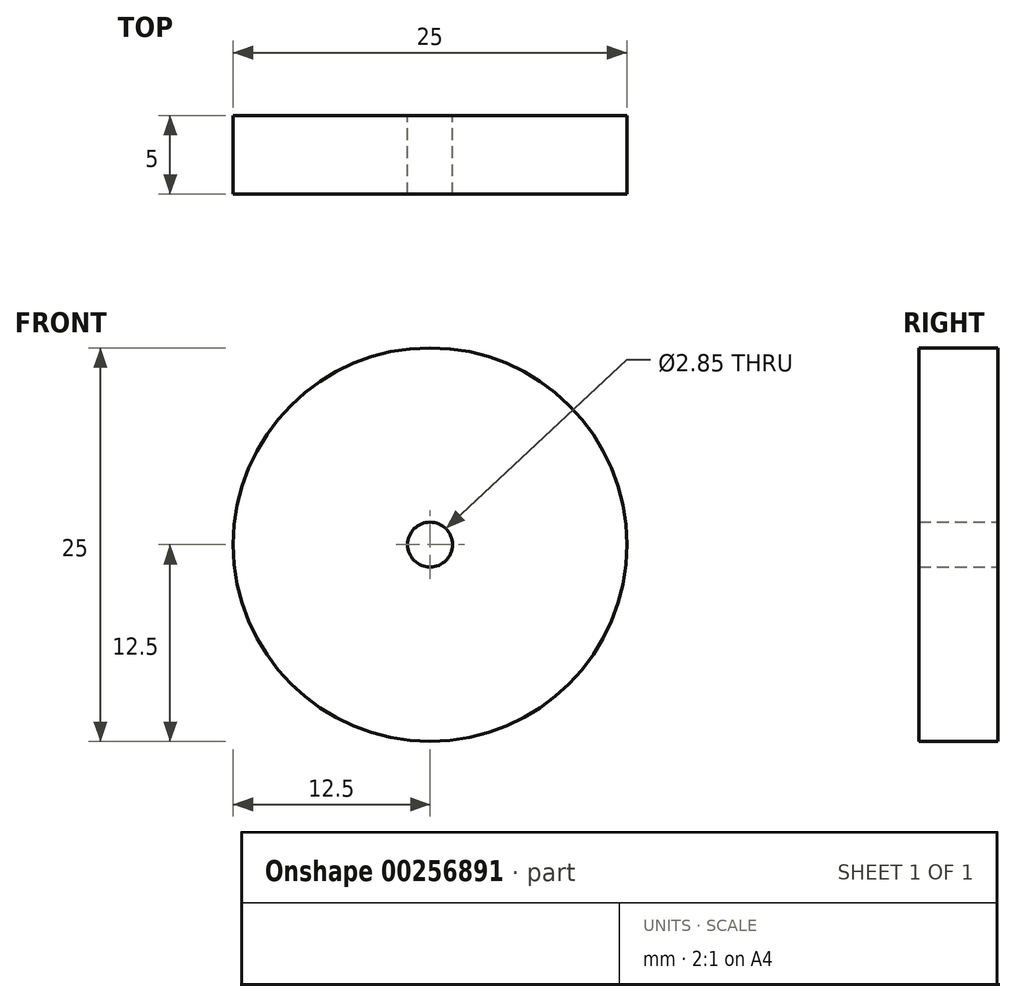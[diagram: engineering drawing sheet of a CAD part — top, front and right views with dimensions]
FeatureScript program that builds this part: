
annotation { "Feature Type Name" : "Feature", "Feature Type Description" : "" }
export const myFeature = defineFeature(function(context is Context, id is Id, definition is map)
    precondition{}
    {
        {
            var Q0;
            Q0=qCreatedBy(makeId("Front.planeOp"),FACE);
            var sketch = newSketch(context, id + "F0", { "sketchPlane" : qUnion([Q0])});
            skCircle(sketch, "E0", {"center": v(0, 0) * mm, "radius": 12.5 * mm});
            skCircle(sketch, "E1", {"center": v(0, 0) * mm, "radius": 1.43 * mm});
            skSolve(sketch);
        }
        {
            var Q0;
            Q0=makeQuery(id+"F0.imprint","IMPRINT",FACE,{"disambiguationData":[TD([[makeQuery(id+"F0.imprint","IMPRINT",EDGE,{"derivedFrom":sQuery(id+"F0.wireOp",EDGE,"E0")}),1.0]])]});
            extrude(context, id + "F1", {"entities" : qUnion([Q0]), "depth" : 5 * mm});
        }
    });
